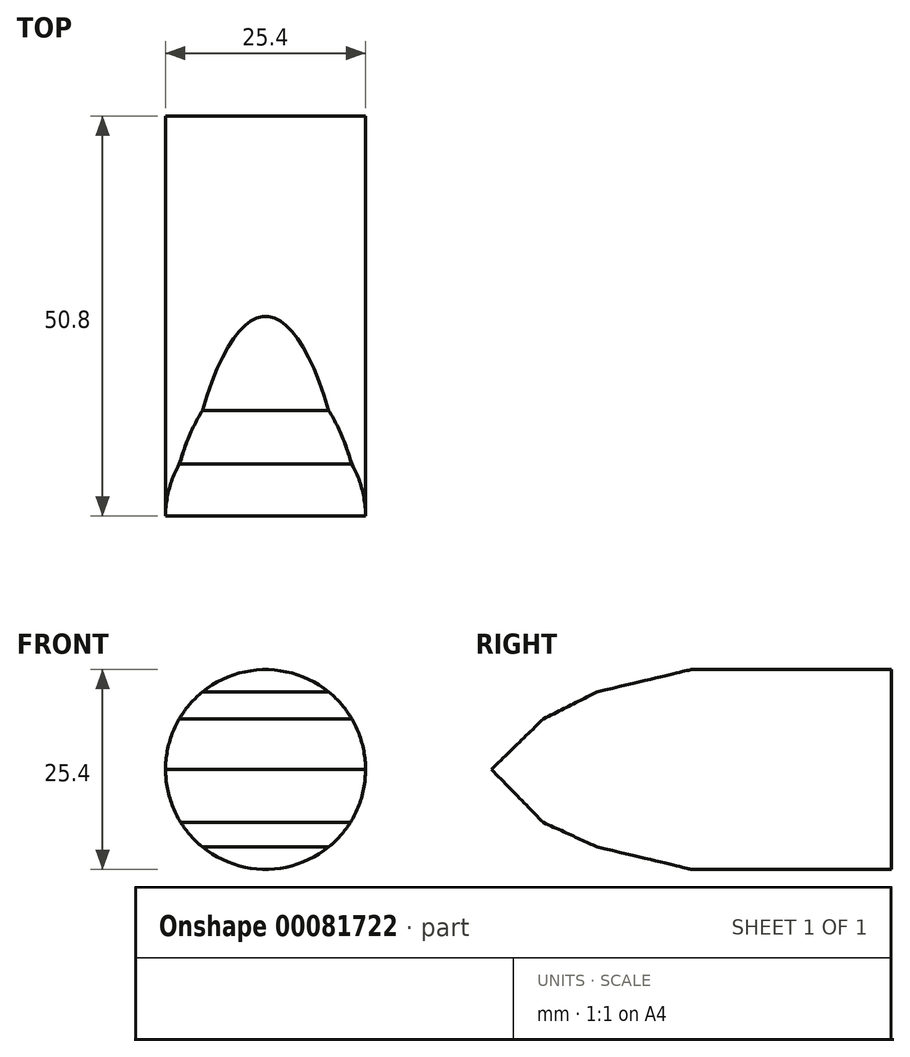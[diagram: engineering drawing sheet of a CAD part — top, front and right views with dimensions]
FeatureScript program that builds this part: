
annotation { "Feature Type Name" : "Feature", "Feature Type Description" : "" }
export const myFeature = defineFeature(function(context is Context, id is Id, definition is map)
    precondition{}
    {
        {
            var Q0;
            Q0=qCreatedBy(makeId("Right.planeOp"),FACE);
            var sketch = newSketch(context, id + "F0", { "sketchPlane" : qUnion([Q0])});
            skLineSegment(sketch, "E0.bottom", {"start": v(25.4, 12.7) * mm, "end": v(-25.4, 12.7) * mm});
            skLineSegment(sketch, "E0.top", {"start": v(25.4, -12.7) * mm, "end": v(-25.4, -12.7) * mm});
            skLineSegment(sketch, "E0.left", {"start": v(25.4, 12.7) * mm, "end": v(25.4, -12.7) * mm});
            skLineSegment(sketch, "E0.right", {"start": v(-25.4, 12.7) * mm, "end": v(-25.4, -12.7) * mm});
            skPoint(sketch, "E0.middle", {"position": v(0, 0) * mm});
            skSolve(sketch);
        }
        {
            var Q0;
            Q0 = qSketchRegion(id + "F0", true);
            extrude(context, id + "F1", {"entities" : qUnion([Q0]), "depth" : 25.4 * mm});
        }
        {
            var Q0;
            Q0=makeQuery(id+"F1.opExtrude","CAP_FACE",FACE,{"disambiguationData":[OSD([sQuery(id+"F0.wireOp",EDGE,"E0.bottom"),sQuery(id+"F0.wireOp",EDGE,"E0.top"),sQuery(id+"F0.wireOp",EDGE,"E0.left"),sQuery(id+"F0.wireOp",EDGE,"E0.right")])],"isStart":false});
            var sketch = newSketch(context, id + "F2", { "sketchPlane" : qUnion([Q0])});
            skLineSegment(sketch, "E1", {"start": v(0, 12.7) * mm, "end": v(-11.98, 9.84) * mm});
            skLineSegment(sketch, "E2", {"start": v(-11.98, 9.84) * mm, "end": v(-18.83, 6.42) * mm});
            skLineSegment(sketch, "E3", {"start": v(-18.83, 6.42) * mm, "end": v(-25.4, 0) * mm});
            skLineSegment(sketch, "E4", {"start": v(-25.4, 0) * mm, "end": v(-18.83, -6.73) * mm});
            skLineSegment(sketch, "E5", {"start": v(-18.83, -6.73) * mm, "end": v(-11.98, -9.84) * mm});
            skLineSegment(sketch, "E6", {"start": v(-11.98, -9.84) * mm, "end": v(0, -12.7) * mm});
            skLineSegment(sketch, "E7", {"start": v(0, -12.7) * mm, "end": v(25.4, -12.7) * mm});
            skLineSegment(sketch, "E8", {"start": v(25.4, -12.7) * mm, "end": v(25.4, 12.7) * mm});
            skLineSegment(sketch, "E9", {"start": v(25.4, 12.7) * mm, "end": v(0, 12.7) * mm});
            skSolve(sketch);
        }
        {
            var Q0;
            {var subQ3=sQuery(id+"F2.wireOp",EDGE,"E1");Q0=makeQuery(id+"F2.imprint","IMPRINT",FACE,{"disambiguationData":[TD([[makeQuery(id+"F2.imprint","IMPRINT",EDGE,{"derivedFrom":subQ3}),-1.0]])]});}
            var Q1;
            {var subQ4=sQuery(id+"F2.wireOp",EDGE,"E4");Q1=makeQuery(id+"F2.imprint","IMPRINT",FACE,{"disambiguationData":[TD([[makeQuery(id+"F2.imprint","IMPRINT",EDGE,{"derivedFrom":subQ4}),-1.0]])]});}
            extrude(context, id + "F3", {"entities" : qUnion([Q0, Q1]), "operationType" : NewBodyOperationType.REMOVE, "oppositeDirection" : true, "depth" : 25.4 * mm});
        }
        {
            var Q0;
            Q0=makeQuery(id+"F3.boolean.opBoolean","COPY",EDGE,{"derivedFrom":makeQuery(id+"F3.opExtrude","CAP_EDGE",EDGE,{"disambiguationData":[OSD([sQuery(id+"F2.wireOp",EDGE,"E3")])],"isStart":true})});
            var Q1;
            Q1=makeQuery(id+"F3.boolean.opBoolean","COPY",EDGE,{"derivedFrom":makeQuery(id+"F3.opExtrude","CAP_EDGE",EDGE,{"disambiguationData":[OSD([sQuery(id+"F2.wireOp",EDGE,"E2")])],"isStart":true})});
            var Q2;
            Q2=makeQuery(id+"F3.boolean.opBoolean","COPY",EDGE,{"derivedFrom":makeQuery(id+"F3.opExtrude","CAP_EDGE",EDGE,{"disambiguationData":[OSD([sQuery(id+"F2.wireOp",EDGE,"E1")])],"isStart":true})});
            var Q3;
            Q3=makeQuery(id+"F1.opExtrude","CAP_EDGE",EDGE,{"disambiguationData":[OSD([sQuery(id+"F0.wireOp",EDGE,"E0.bottom")])],"isStart":false});
            var Q4;
            Q4=makeQuery(id+"F1.opExtrude","CAP_EDGE",EDGE,{"disambiguationData":[OSD([sQuery(id+"F0.wireOp",EDGE,"E0.top")])],"isStart":false});
            var Q5;
            Q5=makeQuery(id+"F3.boolean.opBoolean","COPY",EDGE,{"derivedFrom":makeQuery(id+"F3.opExtrude","CAP_EDGE",EDGE,{"disambiguationData":[OSD([sQuery(id+"F2.wireOp",EDGE,"E6")])],"isStart":true})});
            var Q6;
            Q6=makeQuery(id+"F3.boolean.opBoolean","COPY",EDGE,{"derivedFrom":makeQuery(id+"F3.opExtrude","CAP_EDGE",EDGE,{"disambiguationData":[OSD([sQuery(id+"F2.wireOp",EDGE,"E5")])],"isStart":true})});
            var Q7;
            Q7=makeQuery(id+"F3.boolean.opBoolean","COPY",EDGE,{"derivedFrom":makeQuery(id+"F3.opExtrude","CAP_EDGE",EDGE,{"disambiguationData":[OSD([sQuery(id+"F2.wireOp",EDGE,"E4")])],"isStart":true})});
            var Q8;
            Q8=makeQuery(id+"F1.opExtrude","CAP_EDGE",EDGE,{"disambiguationData":[OSD([sQuery(id+"F0.wireOp",EDGE,"E0.top")])],"isStart":true});
            var Q9;
            Q9=makeQuery(id+"F1.opExtrude","CAP_EDGE",EDGE,{"disambiguationData":[OSD([sQuery(id+"F0.wireOp",EDGE,"E0.bottom")])],"isStart":true});
            var Q10;
            Q10=makeQuery(id+"F3.boolean.opBoolean","COPY",EDGE,{"derivedFrom":makeQuery(id+"F3.opExtrude","CAP_EDGE",EDGE,{"disambiguationData":[OSD([sQuery(id+"F2.wireOp",EDGE,"E1")])],"isStart":false})});
            var Q11;
            Q11=makeQuery(id+"F3.boolean.opBoolean","COPY",EDGE,{"derivedFrom":makeQuery(id+"F3.opExtrude","CAP_EDGE",EDGE,{"disambiguationData":[OSD([sQuery(id+"F2.wireOp",EDGE,"E3")])],"isStart":false})});
            var Q12;
            Q12=makeQuery(id+"F3.boolean.opBoolean","COPY",EDGE,{"derivedFrom":makeQuery(id+"F3.opExtrude","CAP_EDGE",EDGE,{"disambiguationData":[OSD([sQuery(id+"F2.wireOp",EDGE,"E4")])],"isStart":false})});
            var Q13;
            Q13=makeQuery(id+"F3.boolean.opBoolean","COPY",EDGE,{"derivedFrom":makeQuery(id+"F3.opExtrude","CAP_EDGE",EDGE,{"disambiguationData":[OSD([sQuery(id+"F2.wireOp",EDGE,"E5")])],"isStart":false})});
            var Q14;
            Q14=makeQuery(id+"F3.boolean.opBoolean","COPY",EDGE,{"derivedFrom":makeQuery(id+"F3.opExtrude","CAP_EDGE",EDGE,{"disambiguationData":[OSD([sQuery(id+"F2.wireOp",EDGE,"E6")])],"isStart":false})});
            var Q15;
            Q15=makeQuery(id+"F3.boolean.opBoolean","COPY",EDGE,{"derivedFrom":makeQuery(id+"F3.opExtrude","CAP_EDGE",EDGE,{"disambiguationData":[OSD([sQuery(id+"F2.wireOp",EDGE,"E2")])],"isStart":false})});
            fillet(context, id + "F4", {"entities" : qUnion([Q0, Q1, Q2, Q3, Q4, Q5, Q6, Q7, Q8, Q9, Q10, Q11, Q12, Q13, Q14, Q15]), "radius" : 12.7 * mm, "tangentPropagation" : true, "allowEdgeOverflow" : false});
        }
    });
